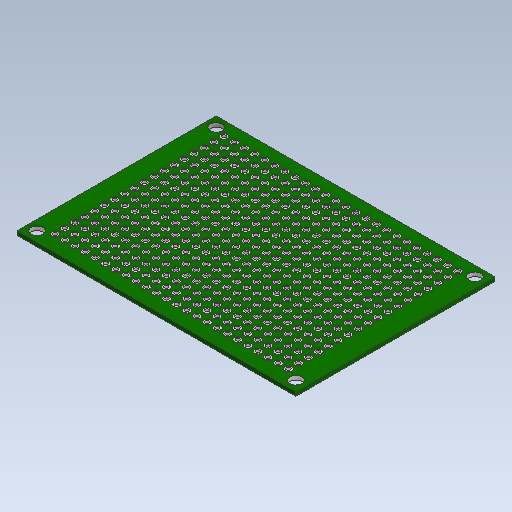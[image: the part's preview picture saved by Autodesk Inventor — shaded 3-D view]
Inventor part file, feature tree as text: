
AUTODESK INVENTOR PART (.ipt)
format: ipt  version: 2021 (Build 250183000, 183)  size: 1,574,912 bytes
history: native  units: mm
features: extrude x4, sketch x3, other x1, pattern_linear x1
ambient origin geometry x8: Origin, YZ Plane, XZ Plane, XY Plane, X Axis, Y Axis, Z Axis, Center Point
bodies: Volumenkörper1 (feature_tree)
feature tree (9):
  other  "Lochrasterplatine50x70"
  extrude  "Extrusion1"  Depth=50.0mm
  extrude  "Extrusion3"  Depth=1.0mm
  extrude  "Extrusion4"  Depth=0.05mm
  extrude  "Extrusion7"  Depth=0.05mm
  pattern_linear  "Rechteckige Anordnung1"  Spacing1=1.0mm  [1 undecoded]
  sketch  "Skizze1"  dims[d0=70.0mm d1=50.0mm]
  sketch  "Skizze3"  dims[d2=1.0mm d3=0.0mm d5=5.5mm]
  sketch  "Skizze4"  dims[d17=3.0mm d18=2.5mm d19=2.5mm d20=1.0mm d21=0.0mm d22=240.0mm d24=2.55mm d25=180.0mm d27=2.5mm d30=1.0mm d31=0.0mm d33=1.75mm d36=240.0mm d38=2.55mm d39=180.0mm d41=2.5mm d44=240.0mm d46=2.55mm d47=180.0mm d49=2.5mm d54=0.05mm d55=0.0mm d56=240.0mm d58=2.55mm d59=180.0mm d61=2.5mm]
note: 1 required parameter value undecoded (feature->parameter linkage not recoverable at this tier; creation-order binding heuristic only, values carry confidence <= 0.55)
